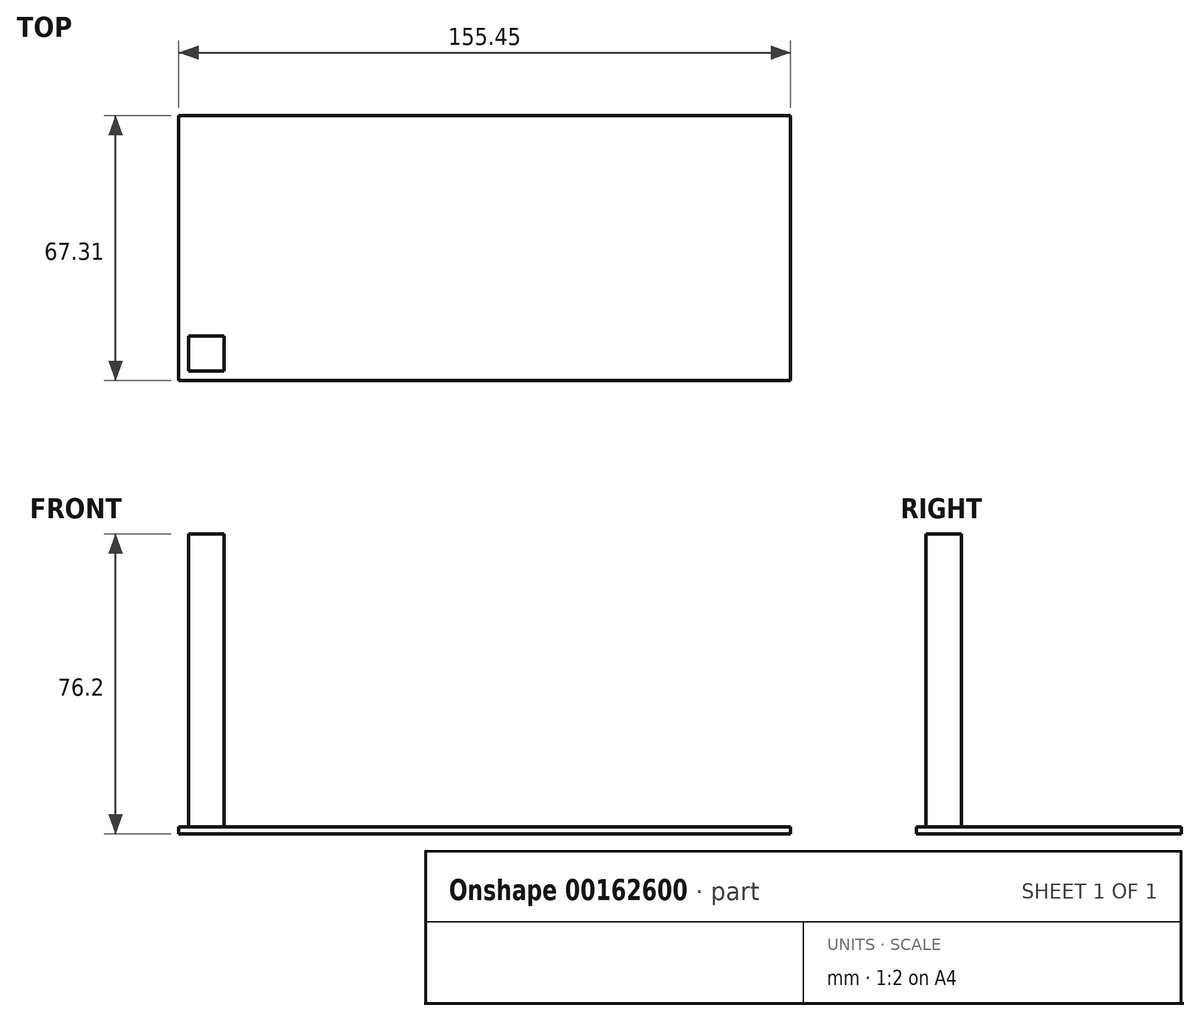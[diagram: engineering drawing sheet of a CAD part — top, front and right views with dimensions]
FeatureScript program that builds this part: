
annotation { "Feature Type Name" : "Feature", "Feature Type Description" : "" }
export const myFeature = defineFeature(function(context is Context, id is Id, definition is map)
    precondition{}
    {
        {
            var Q0;
            Q0=qCreatedBy(makeId("Front.planeOp"),FACE);
            var sketch = newSketch(context, id + "F0", { "sketchPlane" : qUnion([Q0])});
            skLineSegment(sketch, "E0.bottom", {"start": v(-55.06, 32.5) * mm, "end": v(100.39, 32.5) * mm});
            skLineSegment(sketch, "E0.top", {"start": v(-55.06, 30.71) * mm, "end": v(100.39, 30.71) * mm});
            skLineSegment(sketch, "E0.left", {"start": v(-55.06, 32.5) * mm, "end": v(-55.06, 30.71) * mm});
            skLineSegment(sketch, "E0.right", {"start": v(100.39, 32.5) * mm, "end": v(100.39, 30.71) * mm});
            skSolve(sketch);
        }
        {
            var Q0;
            Q0=makeQuery(id+"F0.imprint","IMPRINT",FACE,{"disambiguationData":[TD([[makeQuery(id+"F0.imprint","IMPRINT",EDGE,{"derivedFrom":sQuery(id+"F0.wireOp",EDGE,"E0.bottom")}),-1.0]])]});
            extrude(context, id + "F1", {"entities" : qUnion([Q0]), "depth" : 67.3 * mm});
        }
        {
            var Q0;
            Q0=makeQuery(id+"F1.opExtrude","SWEPT_FACE",FACE,{"disambiguationData":[OSD([sQuery(id+"F0.wireOp",EDGE,"E0.top")])]});
            var sketch = newSketch(context, id + "F2", { "sketchPlane" : qUnion([Q0])});
            skLineSegment(sketch, "E1.bottom", {"start": v(-52.51, 64.9) * mm, "end": v(-43.57, 64.9) * mm});
            skLineSegment(sketch, "E1.top", {"start": v(-52.51, 55.96) * mm, "end": v(-43.57, 55.96) * mm});
            skLineSegment(sketch, "E1.left", {"start": v(-52.51, 64.9) * mm, "end": v(-52.51, 55.96) * mm});
            skLineSegment(sketch, "E1.right", {"start": v(-43.57, 64.9) * mm, "end": v(-43.57, 55.96) * mm});
            skSolve(sketch);
        }
        {
            var Q0;
            Q0 = qSketchRegion(id + "F2", true);
            extrude(context, id + "F3", {"entities" : qUnion([Q0]), "operationType" : NewBodyOperationType.ADD, "oppositeDirection" : true, "depth" : 76.2 * mm});
        }
    });
